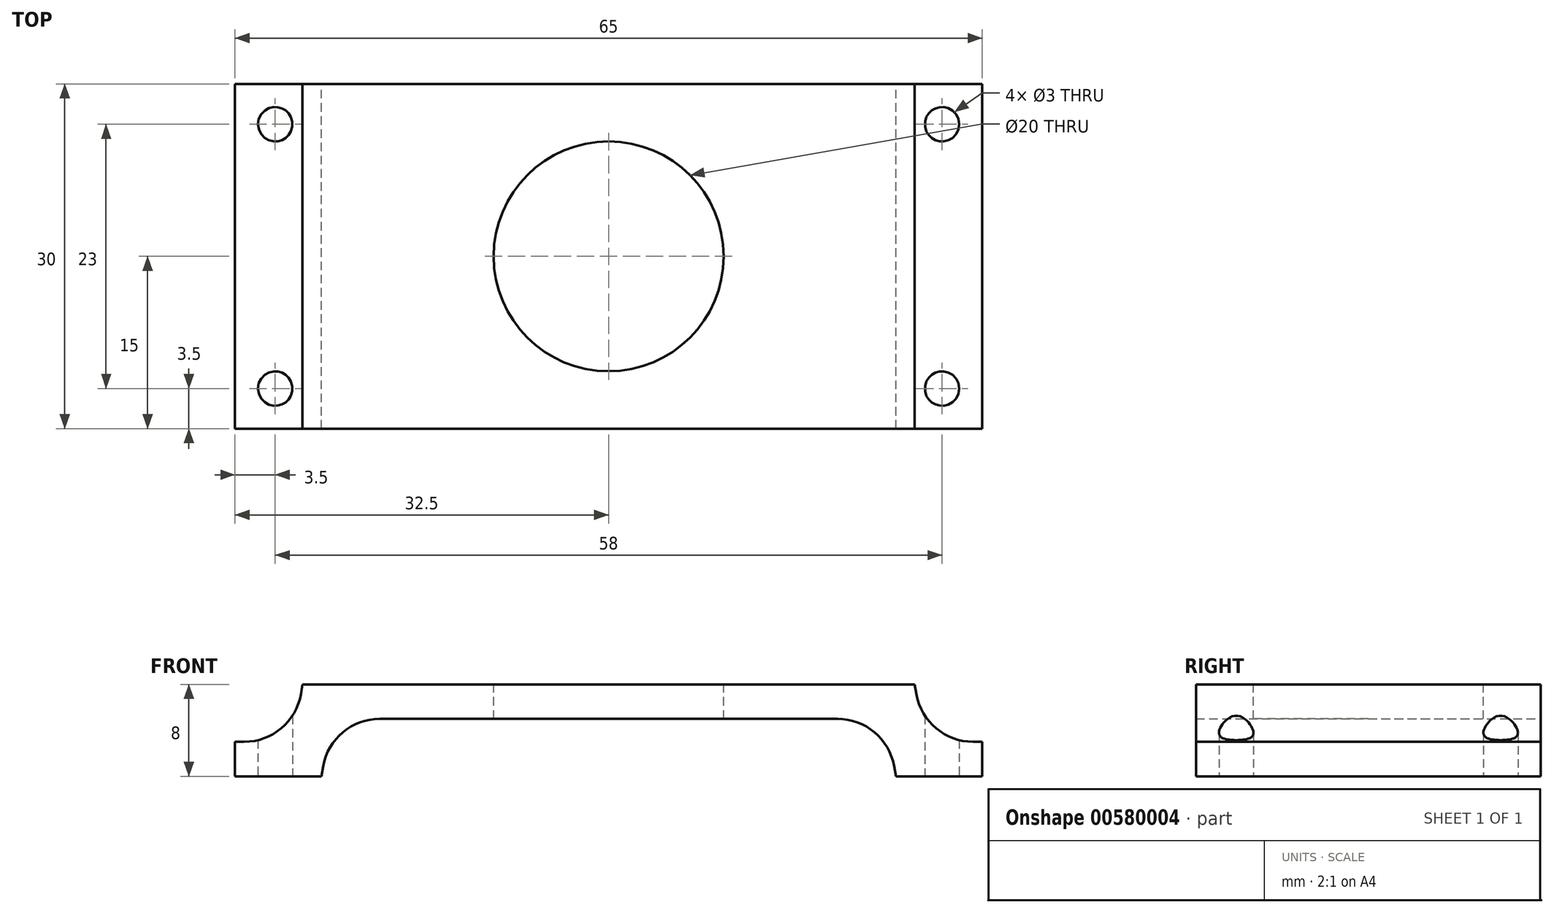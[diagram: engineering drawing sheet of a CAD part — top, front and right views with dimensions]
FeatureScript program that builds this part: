
annotation { "Feature Type Name" : "Feature", "Feature Type Description" : "" }
export const myFeature = defineFeature(function(context is Context, id is Id, definition is map)
    precondition{}
    {
        {
            var Q0;
            Q0=qCreatedBy(makeId("Front.planeOp"),FACE);
            var sketch = newSketch(context, id + "F0", { "sketchPlane" : qUnion([Q0])});
            skLineSegment(sketch, "E0", {"start": v(0, 0) * mm, "end": v(-26.62, 0) * mm});
            skLineSegment(sketch, "E1", {"start": v(-26.62, 0) * mm, "end": v(-26.77, -0.87) * mm});
            skLineSegment(sketch, "E2", {"start": v(-31.7, -5) * mm, "end": v(-32.5, -5) * mm});
            skLineSegment(sketch, "E3.0", {"start": v(-24.98, -8) * mm, "end": v(-32.5, -8) * mm});
            skLineSegment(sketch, "E3.1", {"start": v(-24.83, -7.13) * mm, "end": v(-24.98, -8) * mm});
            skLineSegment(sketch, "E3.2", {"start": v(0, -3) * mm, "end": v(-19.9, -3) * mm});
            skLineSegment(sketch, "E4", {"start": v(-32.5, -5) * mm, "end": v(-32.5, -8) * mm});
            skLineSegment(sketch, "E5", {"start": v(0, -3) * mm, "end": v(0, 0) * mm});
            skPoint(sketch, "E6.visualSharp", {"position": v(-24.1, -3) * mm});
            skArc(sketch, "E6.filletArc", {"start": v(-19.9, -3) * mm, "mid": v(-23.12, -4.17) * mm, "end": v(-24.83, -7.13) * mm});
            skPoint(sketch, "E7.visualSharp", {"position": v(-27.5, -5) * mm});
            skArc(sketch, "E7.filletArc", {"start": v(-31.7, -5) * mm, "mid": v(-28.48, -3.83) * mm, "end": v(-26.77, -0.87) * mm});
            skSolve(sketch);
        }
        {
            var Q0;
            Q0=makeQuery(id+"F0.imprint","IMPRINT",FACE,{"disambiguationData":[TD([[makeQuery(id+"F0.imprint","IMPRINT",EDGE,{"derivedFrom":sQuery(id+"F0.wireOp",EDGE,"E0")}),1.0]])]});
            extrude(context, id + "F1", {"entities" : qUnion([Q0]), "depth" : 30 * mm, "offsetDistance" : 25.4 * mm});
        }
        {
            var Q0;
            Q0=makeQuery(id+"F1.opExtrude","SWEPT_FACE",FACE,{"disambiguationData":[OSD([sQuery(id+"F0.wireOp",EDGE,"E0")])]});
            var sketch = newSketch(context, id + "F2", { "sketchPlane" : qUnion([Q0])});
            skCircle(sketch, "E8", {"center": v(0, -15) * mm, "radius": 10 * mm});
            skSolve(sketch);
        }
        {
            var Q0;
            {var subQ0=sQuery(id+"F2.wireOp",EDGE,"E8");var subQ1=makeQuery(id+"F1.opExtrude","SWEPT_EDGE",EDGE,{"disambiguationData":[OSD([sQuery(id+"F0.wireOp",EDGE,"E0"),sQuery(id+"F0.wireOp",EDGE,"E5")])]});var subQ2=makeQuery(id+"F2.imprint","INTERSECT",VERTEX,{"disambiguationData":[OD(0.0)],"derivedFrom":[subQ1,subQ0]});Q0=makeQuery(id+"F2.imprint","IMPRINT",FACE,{"disambiguationData":[TD([[makeQuery(id+"F2.imprint","IMPRINT",EDGE,{"disambiguationData":[TD([[subQ2,1.0]])],"derivedFrom":subQ0}),1.0]])]});}
            var Q1;
            {var subQ0=sQuery(id+"F2.wireOp",EDGE,"E8");var subQ1=makeQuery(id+"F1.opExtrude","SWEPT_EDGE",EDGE,{"disambiguationData":[OSD([sQuery(id+"F0.wireOp",EDGE,"E0"),sQuery(id+"F0.wireOp",EDGE,"E5")])]});var subQ2=makeQuery(id+"F2.imprint","INTERSECT",VERTEX,{"disambiguationData":[OD(0.0)],"derivedFrom":[subQ1,subQ0]});Q1=makeQuery(id+"F2.imprint","IMPRINT",FACE,{"disambiguationData":[TD([[makeQuery(id+"F2.imprint","IMPRINT",EDGE,{"disambiguationData":[TD([[subQ2,-1.0]])],"derivedFrom":subQ0}),1.0]])]});}
            extrude(context, id + "F3", {"entities" : qUnion([Q0, Q1]), "operationType" : NewBodyOperationType.REMOVE, "endBound" : BoundingType.THROUGH_ALL, "oppositeDirection" : true, "depth" : 25.4 * mm, "offsetDistance" : 25.4 * mm});
        }
        {
            var Q0;
            Q0=makeQuery(id+"F1.opExtrude","SWEPT_FACE",FACE,{"disambiguationData":[OSD([sQuery(id+"F0.wireOp",EDGE,"E3.0")])]});
            var sketch = newSketch(context, id + "F4", { "sketchPlane" : qUnion([Q0])});
            skPoint(sketch, "E9", {"position": v(-29, 26.5) * mm});
            skLineSegment(sketch, "E10", {"start": v(-32.5, 15) * mm, "end": v(0, 15) * mm, "construction": true});
            skPoint(sketch, "E11.MirrorP", {"position": v(-29, 3.5) * mm});
            skSolve(sketch);
        }
        {
            var Q0;
            Q0=sQuery(id+"F4.wireOp",VERTEX,"E9");
            var Q1;
            Q1=sQuery(id+"F4.wireOp",VERTEX,"E11.MirrorP");
            var Q2;
            Q2=makeQuery(id+"F1.opExtrude","SWEPT_BODY",BODY,{"disambiguationData":[OSD([sQuery(id+"F0.wireOp",EDGE,"E0"),sQuery(id+"F0.wireOp",EDGE,"E1"),sQuery(id+"F0.wireOp",EDGE,"E2"),sQuery(id+"F0.wireOp",EDGE,"E3.0"),sQuery(id+"F0.wireOp",EDGE,"E3.1"),sQuery(id+"F0.wireOp",EDGE,"E3.2"),sQuery(id+"F0.wireOp",EDGE,"E4"),sQuery(id+"F0.wireOp",EDGE,"E5"),sQuery(id+"F0.wireOp",EDGE,"E6.filletArc"),sQuery(id+"F0.wireOp",EDGE,"E7.filletArc")])]});
            hole(context, id + "F5", {"style" : HoleStyle.SIMPLE, "endStyle" : HoleEndStyle.THROUGH, "holeDiameter" : 3 * mm, "isTappedThrough" : true, "tappedDepth" : 12 * mm, "tapClearance" : 3, "locations" : qUnion([Q0, Q1]), "scope" : qUnion([Q2])});
        }
        {
            var Q0;
            Q0=makeQuery(id+"F1.opExtrude","SWEPT_BODY",BODY,{"disambiguationData":[OSD([sQuery(id+"F0.wireOp",EDGE,"E0"),sQuery(id+"F0.wireOp",EDGE,"E1"),sQuery(id+"F0.wireOp",EDGE,"E2"),sQuery(id+"F0.wireOp",EDGE,"E3.0"),sQuery(id+"F0.wireOp",EDGE,"E3.1"),sQuery(id+"F0.wireOp",EDGE,"E3.2"),sQuery(id+"F0.wireOp",EDGE,"E4"),sQuery(id+"F0.wireOp",EDGE,"E5"),sQuery(id+"F0.wireOp",EDGE,"E6.filletArc"),sQuery(id+"F0.wireOp",EDGE,"E7.filletArc")])]});
            var Q1;
            Q1=qCreatedBy(makeId("Right.planeOp"),FACE);
            mirror(context, id + "F6", {"operationType" : NewBodyOperationType.ADD, "entities" : qUnion([Q0]), "mirrorPlane" : qUnion([Q1])});
        }
    });
